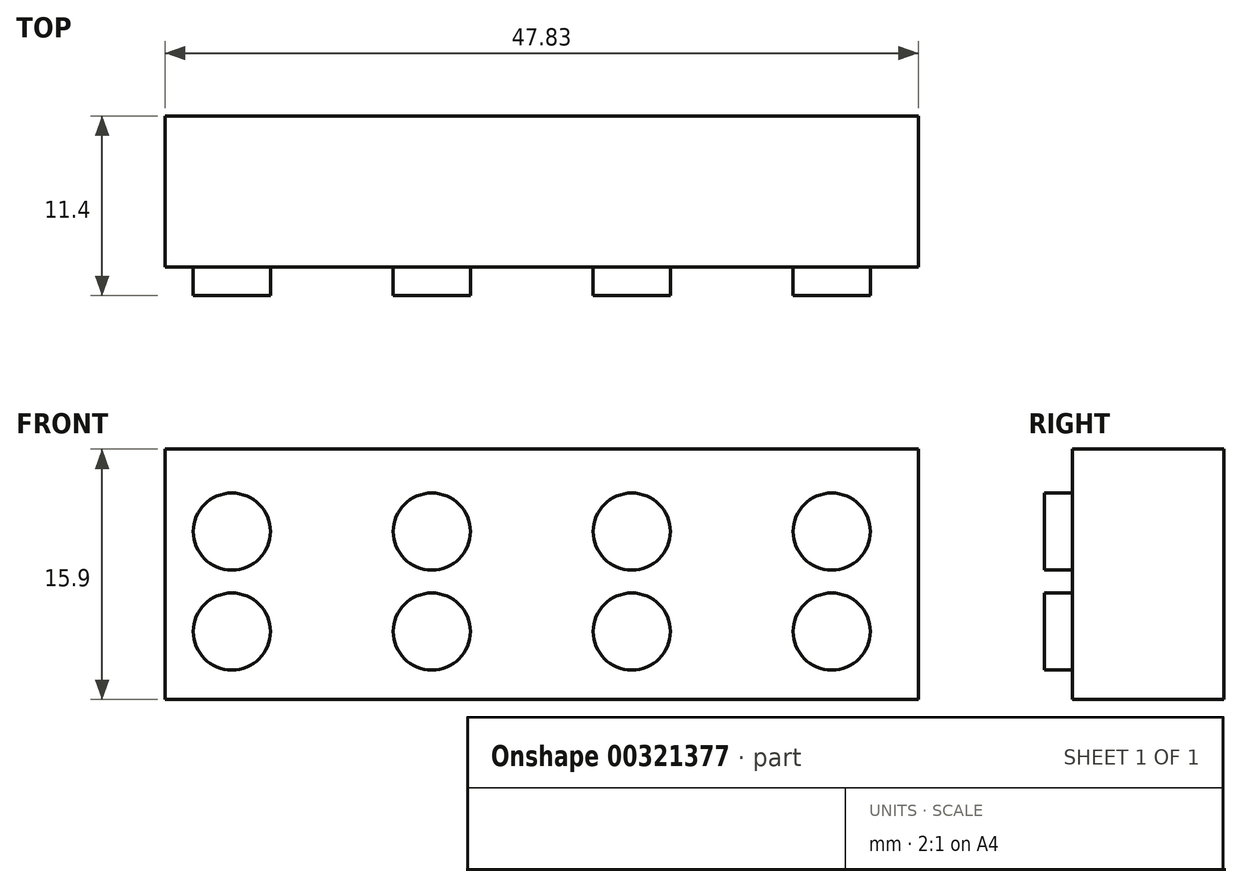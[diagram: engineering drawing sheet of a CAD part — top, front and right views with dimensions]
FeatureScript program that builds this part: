
annotation { "Feature Type Name" : "Feature", "Feature Type Description" : "" }
export const myFeature = defineFeature(function(context is Context, id is Id, definition is map)
    precondition{}
    {
        {
            var Q0;
            Q0=qCreatedBy(makeId("Front.planeOp"),FACE);
            var sketch = newSketch(context, id + "F0", { "sketchPlane" : qUnion([Q0])});
            skLineSegment(sketch, "E0.bottom", {"start": v(-47.83, 15.9) * mm, "end": v(0, 15.9) * mm});
            skLineSegment(sketch, "E0.top", {"start": v(-47.83, 0) * mm, "end": v(0, 0) * mm});
            skLineSegment(sketch, "E0.left", {"start": v(-47.83, 15.9) * mm, "end": v(-47.83, 0) * mm});
            skLineSegment(sketch, "E0.right", {"start": v(0, 15.9) * mm, "end": v(0, 0) * mm});
            skSolve(sketch);
        }
        {
            var Q0;
            Q0=makeQuery(id+"F0.imprint","IMPRINT",FACE,{"disambiguationData":[TD([[makeQuery(id+"F0.imprint","IMPRINT",EDGE,{"derivedFrom":sQuery(id+"F0.wireOp",EDGE,"E0.bottom")}),-1.0]])]});
            extrude(context, id + "F1", {"entities" : qUnion([Q0]), "depth" : 9.6 * mm});
        }
        {
            var Q0;
            Q0=makeQuery(id+"F1.opExtrude","CAP_FACE",FACE,{"disambiguationData":[OSD([sQuery(id+"F0.wireOp",EDGE,"E0.bottom"),sQuery(id+"F0.wireOp",EDGE,"E0.top"),sQuery(id+"F0.wireOp",EDGE,"E0.left"),sQuery(id+"F0.wireOp",EDGE,"E0.right")])],"isStart":false});
            var sketch = newSketch(context, id + "F2", { "sketchPlane" : qUnion([Q0])});
            skCircle(sketch, "E1", {"center": v(-5.5, 10.66) * mm, "radius": 2.45 * mm});
            skCircle(sketch, "E2.0.1.0", {"center": v(-5.5, 4.3) * mm, "radius": 2.45 * mm});
            skCircle(sketch, "E2.1.0.0", {"center": v(-18.2, 10.66) * mm, "radius": 2.45 * mm});
            skCircle(sketch, "E2.1.1.0", {"center": v(-18.2, 4.3) * mm, "radius": 2.45 * mm});
            skCircle(sketch, "E2.2.0.0", {"center": v(-30.9, 10.66) * mm, "radius": 2.45 * mm});
            skCircle(sketch, "E2.2.1.0", {"center": v(-30.9, 4.3) * mm, "radius": 2.45 * mm});
            skCircle(sketch, "E2.3.0.0", {"center": v(-43.6, 10.66) * mm, "radius": 2.45 * mm});
            skCircle(sketch, "E2.3.1.0", {"center": v(-43.6, 4.3) * mm, "radius": 2.45 * mm});
            skLineSegment(sketch, "E2.direction1", {"start": v(-5.25, 10.66) * mm, "end": v(-17.95, 10.66) * mm, "construction": true});
            skLineSegment(sketch, "E2.direction2", {"start": v(-5.25, 10.66) * mm, "end": v(-5.25, 4.3) * mm, "construction": true});
            skSolve(sketch);
        }
        {
            var Q0;
            Q0 = qSketchRegion(id + "F2", true);
            extrude(context, id + "F3", {"entities" : qUnion([Q0]), "operationType" : NewBodyOperationType.ADD, "depth" : 1.8 * mm});
        }
    });
